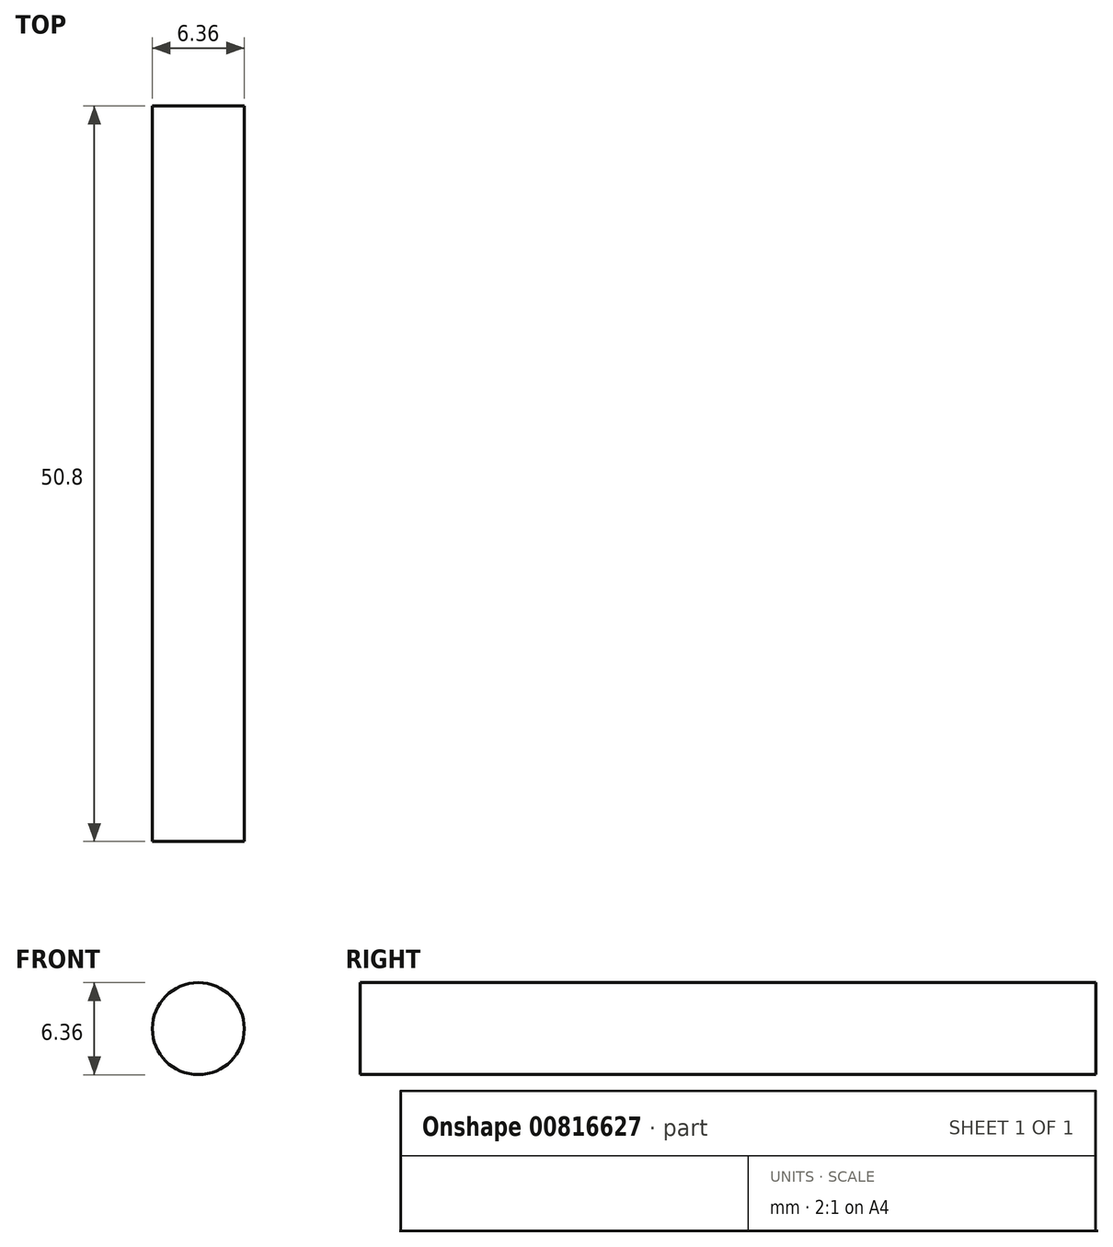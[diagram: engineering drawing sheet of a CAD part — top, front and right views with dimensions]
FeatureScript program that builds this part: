
annotation { "Feature Type Name" : "Feature", "Feature Type Description" : "" }
export const myFeature = defineFeature(function(context is Context, id is Id, definition is map)
    precondition{}
    {
        {
            var Q0;
            Q0=qCreatedBy(makeId("Front.planeOp"),FACE);
            var sketch = newSketch(context, id + "F0", { "sketchPlane" : qUnion([Q0])});
            skCircle(sketch, "E0", {"center": v(0, 0) * mm, "radius": 3.18 * mm});
            skSolve(sketch);
        }
        {
            var Q0;
            Q0 = qSketchRegion(id + "F0", true);
            extrude(context, id + "F1", {"entities" : qUnion([Q0]), "endBound" : BoundingType.SYMMETRIC, "depth" : 50.8 * mm, "offsetDistance" : 25.4 * mm});
        }
    });
